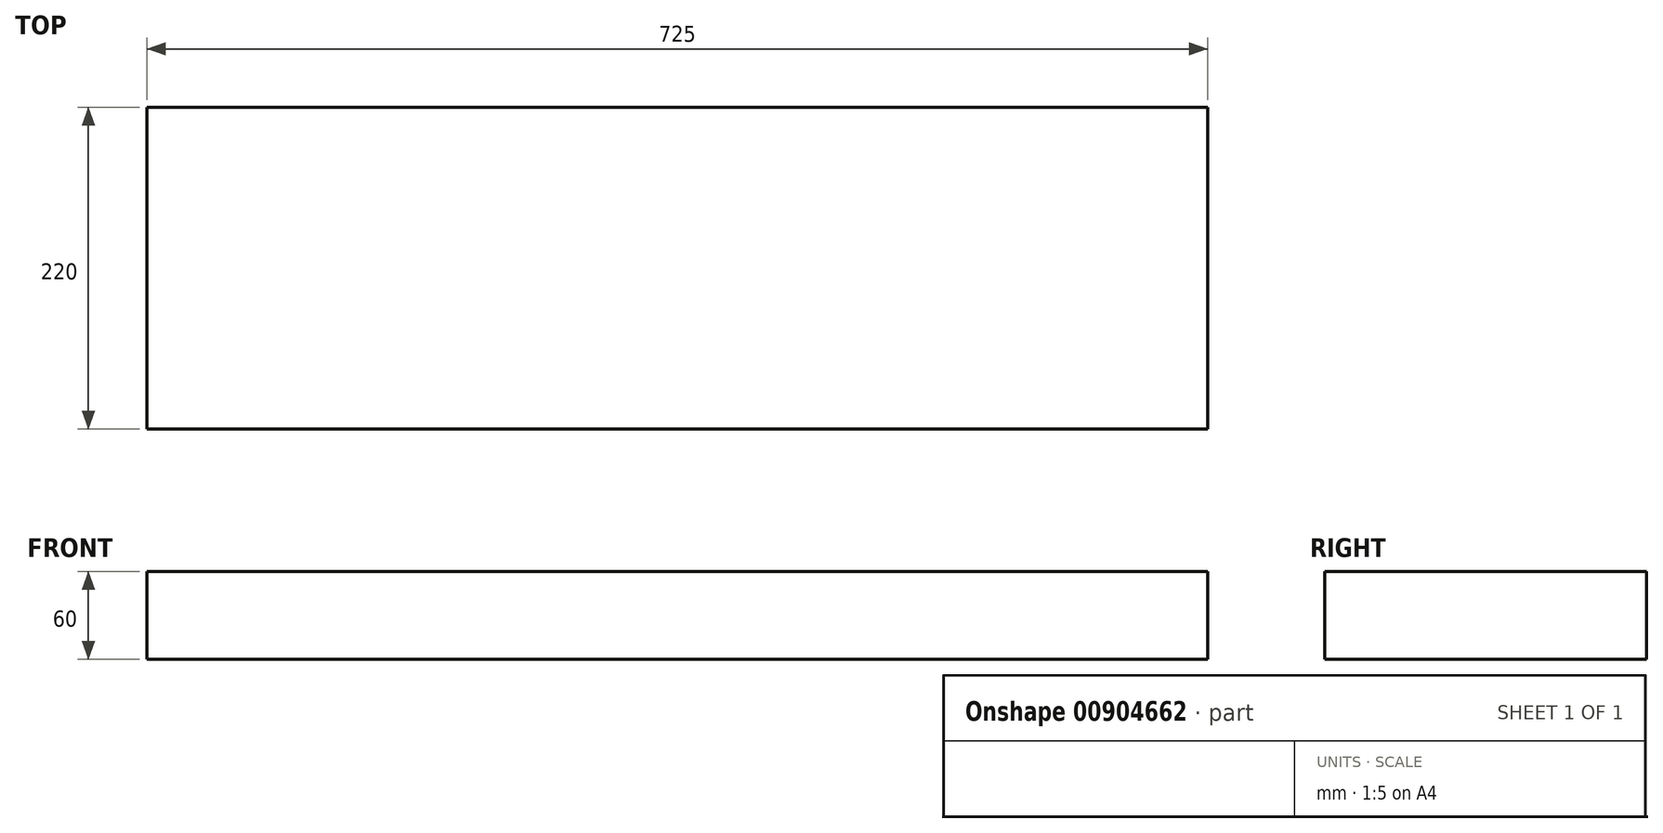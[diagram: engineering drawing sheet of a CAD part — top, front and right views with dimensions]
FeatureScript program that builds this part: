
annotation { "Feature Type Name" : "Feature", "Feature Type Description" : "" }
export const myFeature = defineFeature(function(context is Context, id is Id, definition is map)
    precondition{}
    {
        {
            var Q0;
            Q0=qCreatedBy(makeId("Top.planeOp"),FACE);
            var sketch = newSketch(context, id + "F0", { "sketchPlane" : qUnion([Q0])});
            skLineSegment(sketch, "E0.bottom", {"start": v(0, 0) * mm, "end": v(-725, 0) * mm});
            skLineSegment(sketch, "E0.top", {"start": v(0, 220) * mm, "end": v(-725, 220) * mm});
            skLineSegment(sketch, "E0.left", {"start": v(0, 0) * mm, "end": v(0, 220) * mm});
            skLineSegment(sketch, "E0.right", {"start": v(-725, 0) * mm, "end": v(-725, 220) * mm});
            skSolve(sketch);
        }
        {
            var Q0;
            Q0=qSketchRegion(id+"F0",true);
            extrude(context, id + "F1", {"entities" : qUnion([Q0]), "depth" : 60 * mm, "offsetDistance" : 25 * mm});
        }
    });
